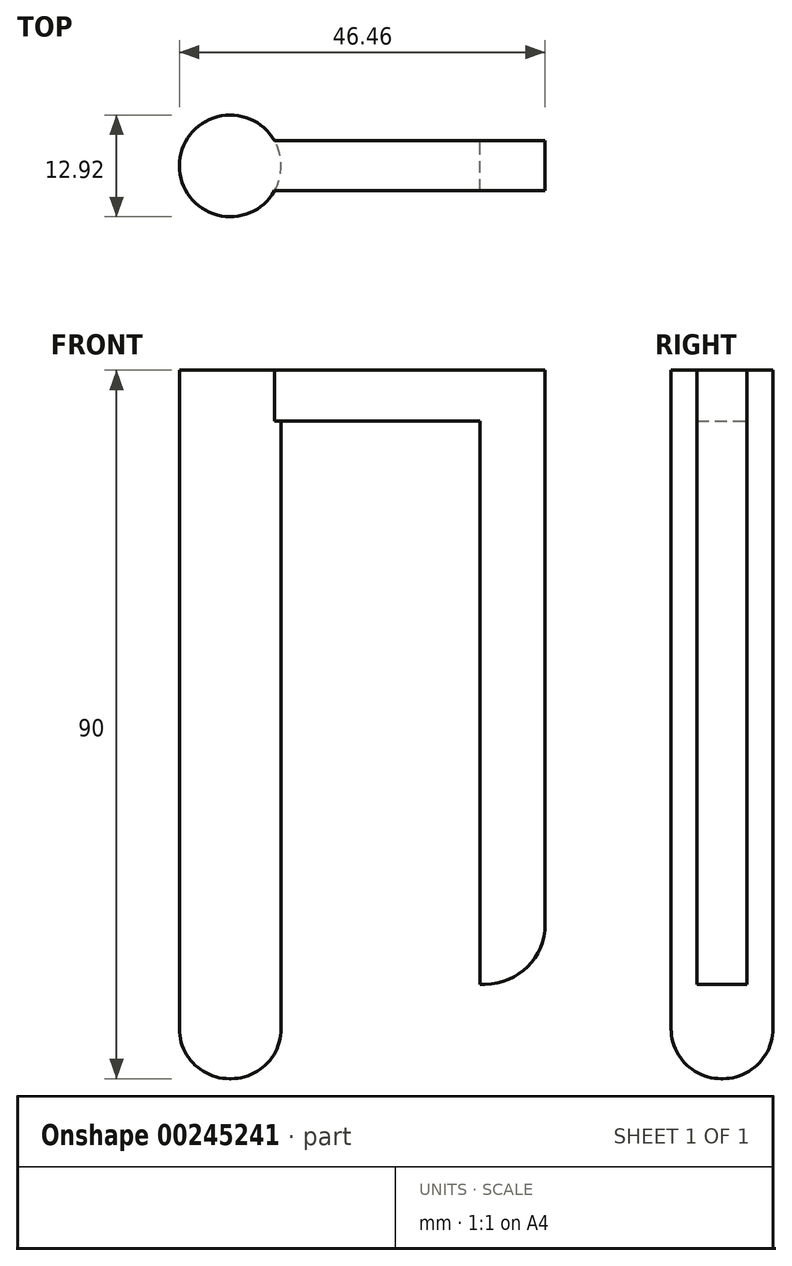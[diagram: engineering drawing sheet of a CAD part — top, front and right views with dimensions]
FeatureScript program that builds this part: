
annotation { "Feature Type Name" : "Feature", "Feature Type Description" : "" }
export const myFeature = defineFeature(function(context is Context, id is Id, definition is map)
    precondition{}
    {
        {
            var Q0;
            Q0=qCreatedBy(makeId("Front.planeOp"),FACE);
            var sketch = newSketch(context, id + "F0", { "sketchPlane" : qUnion([Q0])});
            skLineSegment(sketch, "E0.top", {"start": v(0, 76.98) * mm, "end": v(6.46, 76.98) * mm});
            skLineSegment(sketch, "E0.left", {"start": v(0, 0) * mm, "end": v(0, 76.98) * mm});
            skLineSegment(sketch, "E0.right", {"start": v(6.46, -0.21) * mm, "end": v(6.46, 76.98) * mm});
            skLineSegment(sketch, "E1", {"start": v(0, 0) * mm, "end": v(0, -6.56) * mm});
            skLineSegment(sketch, "E2", {"start": v(0, -6.56) * mm, "end": v(0.1, -6.56) * mm});
            skPoint(sketch, "E3.visualSharp", {"position": v(6.46, -6.56) * mm});
            skArc(sketch, "E3.filletArc", {"start": v(0.1, -6.56) * mm, "mid": v(4.6, -4.7) * mm, "end": v(6.46, -0.21) * mm});
            skLineSegment(sketch, "E4.left", {"start": v(6.46, 83.44) * mm, "end": v(6.46, 76.98) * mm});
            skLineSegment(sketch, "E5.bottom", {"start": v(0, 76.98) * mm, "end": v(31.7, 76.98) * mm});
            skLineSegment(sketch, "E5.top", {"start": v(0, 83.44) * mm, "end": v(31.7, 83.44) * mm});
            skLineSegment(sketch, "E5.left", {"start": v(0, 83.44) * mm, "end": v(0, 76.98) * mm});
            skLineSegment(sketch, "E5.right", {"start": v(31.7, 83.44) * mm, "end": v(31.7, 76.98) * mm});
            skLineSegment(sketch, "E6.bottom", {"start": v(31.7, 76.98) * mm, "end": v(40, 76.98) * mm});
            skLineSegment(sketch, "E6.top", {"start": v(31.7, 5.42) * mm, "end": v(32.38, 5.42) * mm});
            skLineSegment(sketch, "E6.left", {"start": v(31.7, 76.98) * mm, "end": v(31.7, 5.42) * mm});
            skLineSegment(sketch, "E6.right", {"start": v(40, 76.98) * mm, "end": v(40, 13.04) * mm});
            skPoint(sketch, "E7.visualSharp", {"position": v(40, 5.42) * mm});
            skArc(sketch, "E7.filletArc", {"start": v(32.38, 5.42) * mm, "mid": v(37.77, 7.65) * mm, "end": v(40, 13.04) * mm});
            skLineSegment(sketch, "E8.bottom", {"start": v(31.7, 83.44) * mm, "end": v(40, 83.44) * mm});
            skLineSegment(sketch, "E8.right", {"start": v(40, 83.44) * mm, "end": v(40, 76.98) * mm});
            skSolve(sketch);
        }
        {
            var Q0;
            {var subQ2=sQuery(id+"F0.wireOp",EDGE,"E0.left");Q0=makeQuery(id+"F0.imprint","IMPRINT",FACE,{"disambiguationData":[TD([[makeQuery(id+"F0.imprint","IMPRINT",EDGE,{"derivedFrom":subQ2}),-1.0]])]});}
            var Q1;
            {var subQ0=sQuery(id+"F0.wireOp",EDGE,"E4.left");Q1=makeQuery(id+"F0.imprint","IMPRINT",FACE,{"disambiguationData":[TD([[makeQuery(id+"F0.imprint","IMPRINT",EDGE,{"derivedFrom":subQ0}),-1.0]])]});}
            var Q2;
            Q2=sQuery(id+"F0.wireOp",EDGE,"E0.left");
            revolve(context, id + "F1", {"entities" : qUnion([Q0, Q1]), "axis" : qUnion([Q2]), "revolveType" : RevolveType.FULL});
        }
        {
            var Q0;
            {var subQ0=sQuery(id+"F0.wireOp",EDGE,"E4.left");Q0=makeQuery(id+"F0.imprint","IMPRINT",FACE,{"disambiguationData":[TD([[makeQuery(id+"F0.imprint","IMPRINT",EDGE,{"derivedFrom":subQ0}),1.0]])]});}
            var Q1;
            {var subQ0=sQuery(id+"F0.wireOp",EDGE,"E4.left");Q1=makeQuery(id+"F0.imprint","IMPRINT",FACE,{"disambiguationData":[TD([[makeQuery(id+"F0.imprint","IMPRINT",EDGE,{"derivedFrom":subQ0}),-1.0]])]});}
            var Q2;
            Q2=makeQuery(id+"F0.imprint","IMPRINT",FACE,{"disambiguationData":[TD([[makeQuery(id+"F0.imprint","IMPRINT",EDGE,{"derivedFrom":sQuery(id+"F0.wireOp",EDGE,"E8.bottom")}),-1.0]])]});
            var Q3;
            Q3=makeQuery(id+"F0.imprint","IMPRINT",FACE,{"disambiguationData":[TD([[makeQuery(id+"F0.imprint","IMPRINT",EDGE,{"derivedFrom":sQuery(id+"F0.wireOp",EDGE,"E6.top")}),1.0]])]});
            extrude(context, id + "F2", {"entities" : qUnion([Q0, Q1, Q2, Q3]), "operationType" : NewBodyOperationType.ADD, "endBound" : BoundingType.SYMMETRIC, "depth" : 6.35 * mm});
        }
    });
